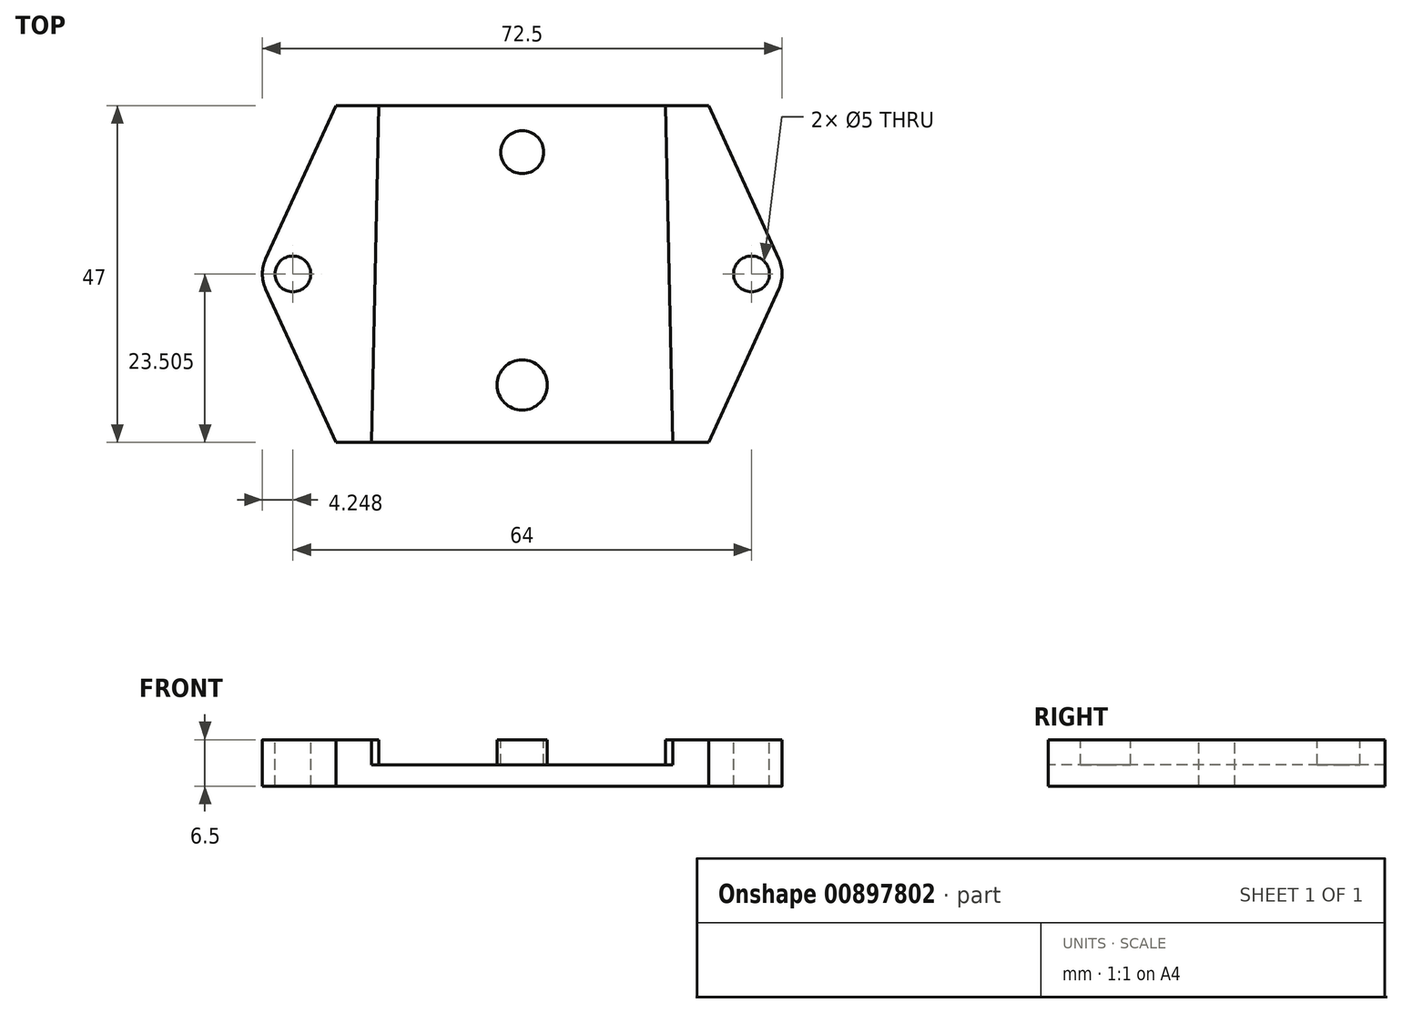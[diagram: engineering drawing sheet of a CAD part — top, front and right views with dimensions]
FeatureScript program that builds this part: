
annotation { "Feature Type Name" : "Feature", "Feature Type Description" : "" }
export const myFeature = defineFeature(function(context is Context, id is Id, definition is map)
    precondition{}
    {
        {
            var Q0;
            Q0=qCreatedBy(makeId("Top.planeOp"),FACE);
            var sketch = newSketch(context, id + "F0", { "sketchPlane" : qUnion([Q0])});
            skLineSegment(sketch, "E0.bottom", {"start": v(-22.7, 19.47) * mm, "end": v(29.3, 19.47) * mm});
            skLineSegment(sketch, "E0.top", {"start": v(-22.7, -27.53) * mm, "end": v(29.3, -27.53) * mm});
            skLineSegment(sketch, "E1", {"start": v(-22.7, 19.47) * mm, "end": v(-33.45, -4.03) * mm});
            skLineSegment(sketch, "E2", {"start": v(-33.45, -4.03) * mm, "end": v(-22.7, -27.53) * mm});
            skLineSegment(sketch, "E3", {"start": v(29.3, 19.47) * mm, "end": v(40.05, -4.03) * mm});
            skLineSegment(sketch, "E4", {"start": v(40.05, -4.03) * mm, "end": v(29.3, -27.53) * mm});
            skCircle(sketch, "E5", {"center": v(35.3, -4.03) * mm, "radius": 2.5 * mm});
            skCircle(sketch, "E6", {"center": v(-28.7, -4.03) * mm, "radius": 2.5 * mm});
            skLineSegment(sketch, "E7", {"start": v(-16.7, 19.47) * mm, "end": v(-17.7, -27.53) * mm});
            skLineSegment(sketch, "E8", {"start": v(23.3, 19.47) * mm, "end": v(24.3, -27.53) * mm});
            skCircle(sketch, "E9", {"center": v(3.3, 12.97) * mm, "radius": 3 * mm});
            skCircle(sketch, "E10", {"center": v(3.3, -19.53) * mm, "radius": 3.5 * mm});
            skSolve(sketch);
        }
        {
            var Q0;
            Q0 = qSketchRegion(id + "F0", true);
            var Q1;
            Q1=makeQuery(id+"F0.imprint","IMPRINT",FACE,{"disambiguationData":[TD([[makeQuery(id+"F0.imprint","IMPRINT",EDGE,{"derivedFrom":sQuery(id+"F0.wireOp",EDGE,"E9")}),1.0]])]});
            var Q2;
            Q2=makeQuery(id+"F0.imprint","IMPRINT",FACE,{"disambiguationData":[TD([[makeQuery(id+"F0.imprint","IMPRINT",EDGE,{"derivedFrom":sQuery(id+"F0.wireOp",EDGE,"E10")}),1.0]])]});
            extrude(context, id + "F1", {"entities" : qUnion([Q0, Q1, Q2]), "oppositeDirection" : true, "depth" : 6.5 * mm, "offsetDistance" : 25 * mm});
        }
        {
            var Q0;
            {var subQ1=sQuery(id+"F0.wireOp",EDGE,"E7");Q0=makeQuery(id+"F0.imprint","IMPRINT",FACE,{"disambiguationData":[TD([[makeQuery(id+"F0.imprint","IMPRINT",EDGE,{"derivedFrom":subQ1}),1.0]])]});}
            extrude(context, id + "F2", {"entities" : qUnion([Q0]), "operationType" : NewBodyOperationType.REMOVE, "oppositeDirection" : true, "depth" : 3.5 * mm, "offsetDistance" : 25 * mm});
        }
        {
            var Q0;
            Q0=makeQuery(id+"F1.opExtrude","SWEPT_EDGE",EDGE,{"disambiguationData":[OSD([sQuery(id+"F0.wireOp",EDGE,"E1"),sQuery(id+"F0.wireOp",EDGE,"E2")])]});
            var Q1;
            Q1=makeQuery(id+"F1.opExtrude","SWEPT_EDGE",EDGE,{"disambiguationData":[OSD([sQuery(id+"F0.wireOp",EDGE,"E3"),sQuery(id+"F0.wireOp",EDGE,"E4")])]});
            fillet(context, id + "F3", {"entities" : qUnion([Q0, Q1]), "radius" : 5 * mm, "tangentPropagation" : true, "allowEdgeOverflow" : false});
        }
    });
